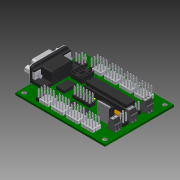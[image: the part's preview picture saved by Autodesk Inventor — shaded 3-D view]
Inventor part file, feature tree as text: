
AUTODESK INVENTOR PART (.ipt)
format: ipt  version: 2015 (Build 190159000, 159)  size: 3,395,584 bytes
history: native  units: in
note: dims shown in document units (in); Inventor stores cm internally (conversion verified against a paired STEP export)
features: imported_body x155, other x125, chamfer x18, extrude x11, sketch x2, fillet x1, revolve x1, mirror x1
ambient origin geometry x8: Origin, YZ Plane, XZ Plane, XY Plane, X Axis, Y Axis, Z Axis, Center Point
bodies: Body1 (feature_tree), Body2 (feature_tree), Body3 (feature_tree), Body4 (feature_tree), Body5 (feature_tree), Body6 (feature_tree), Body7 (feature_tree), Body8 (feature_tree), Body9 (feature_tree), Body10 (feature_tree), Body11 (feature_tree), Body12 (feature_tree), Body13 (feature_tree), Body14 (feature_tree), Body15 (feature_tree), Body16 (feature_tree), Body17 (feature_tree), Body18 (feature_tree), Body19 (feature_tree), Body20 (feature_tree), Body21 (feature_tree), Body22 (feature_tree), Body23 (feature_tree), Body24 (feature_tree), Body25 (feature_tree), Body26 (feature_tree), Body27 (feature_tree), Body28 (feature_tree), Body29 (feature_tree), Body30 (feature_tree), Body31 (feature_tree), Body32 (feature_tree), Body33 (feature_tree), Body34 (feature_tree), Body35 (feature_tree), Body36 (feature_tree), Body37 (feature_tree), Body38 (feature_tree), Body39 (feature_tree), Body40 (feature_tree), Body41 (feature_tree), Body42 (feature_tree), Body43 (feature_tree), Body44 (feature_tree), Body45 (feature_tree), Body46 (feature_tree), Body47 (feature_tree), Body48 (feature_tree), Body49 (feature_tree), Body50 (feature_tree), Body51 (feature_tree), Body52 (feature_tree), Body53 (feature_tree), Body54 (feature_tree), Body55 (feature_tree), Body56 (feature_tree), Body57 (feature_tree), Body58 (feature_tree), Body59 (feature_tree), Body60 (feature_tree), Body61 (feature_tree), Body62 (feature_tree), Body63 (feature_tree), Body64 (feature_tree), Body65 (feature_tree), Body66 (feature_tree), Body67 (feature_tree), Body68 (feature_tree), Body69 (feature_tree), Body70 (feature_tree), Body71 (feature_tree), Body72 (feature_tree), Body73 (feature_tree), Body74 (feature_tree), Body75 (feature_tree), Body76 (feature_tree), Body77 (feature_tree), Body78 (feature_tree), Body79 (feature_tree), Body80 (feature_tree), Body81 (feature_tree), Body82 (feature_tree), Body83 (feature_tree), Body84 (feature_tree), Body85 (feature_tree), Body86 (feature_tree), Body87 (feature_tree), Body88 (feature_tree), Body89 (feature_tree), Body90 (feature_tree), Body91 (feature_tree), Body92 (feature_tree), Body93 (feature_tree), Body94 (feature_tree), Body95 (feature_tree), Body96 (feature_tree), Body97 (feature_tree), Body98 (feature_tree), Body99 (feature_tree), Body100 (feature_tree), Body101 (feature_tree), Body102 (feature_tree), Body103 (feature_tree), Body104 (feature_tree), Body105 (feature_tree), Body106 (feature_tree), Body107 (feature_tree), Body108 (feature_tree), Body109 (feature_tree), Body110 (feature_tree), Body111 (feature_tree), Body112 (feature_tree), Body113 (feature_tree), Body114 (feature_tree), Body115 (feature_tree), Body116 (feature_tree), Body117 (feature_tree), Body118 (feature_tree), Body119 (feature_tree), Body120 (feature_tree), Body121 (feature_tree), Body122 (feature_tree), Body123 (feature_tree), Body124 (feature_tree), Body125 (feature_tree), Body126 (feature_tree), Body127 (feature_tree), Body128 (feature_tree), Body129 (feature_tree), Body130 (feature_tree), Body131 (feature_tree), Body132 (feature_tree), Body133 (feature_tree), Body134 (feature_tree), Body135 (feature_tree), Body136 (feature_tree), Body137 (feature_tree), Body138 (feature_tree), Body139 (feature_tree), Body140 (feature_tree), Body141 (feature_tree), Body142 (feature_tree), Body143 (feature_tree), Body144 (feature_tree), Body145 (feature_tree), Body146 (feature_tree), Body147 (feature_tree), Body148 (feature_tree), Body149 (feature_tree), Body150 (feature_tree), Body151 (feature_tree), Body152 (feature_tree), Body153 (feature_tree), Body154 (feature_tree), Body155 (feature_tree)
feature tree (314):
  chamfer  "Chamfer1"  Distance=1.0039in
  other  "ssc-321"
  sketch  "Sketch1"  dims[d2=0.1378in]
  extrude  "Extrusion1"  Depth=1.0in
  chamfer  "Chamfer2"  Distance=0.1378in
  other  "LPattern2[4]"
  other  "LPattern2[5]"
  other  "LPattern2[6]"
  other  "LPattern2[7]"
  other  "LPattern2[8]"
  other  "LPattern2[9]"
  other  "LPattern2[10]"
  other  "LPattern2[11]"
  other  "LPattern2[12]"
  other  "LPattern2[13]"
  other  "LPattern2[14]"
  other  "LPattern2[15]"
  other  "LPattern2[16]"
  other  "LPattern2[20]"
  other  "LPattern2[21]"
  other  "LPattern2[22]"
  other  "LPattern2[23]"
  other  "LPattern2[24]"
  other  "LPattern2[25]"
  other  "LPattern2[26]"
  other  "LPattern2[27]"
  other  "LPattern2[28]"
  other  "LPattern2[29]"
  other  "LPattern2[30]"
  other  "LPattern2[31]"
  other  "LPattern2[32]"
  other  "LPattern2[36]"
  other  "LPattern2[37]"
  other  "LPattern2[38]"
  other  "LPattern2[39]"
  other  "LPattern2[40]"
  other  "LPattern2[41]"
  other  "LPattern2[42]"
  other  "LPattern2[43]"
  other  "LPattern2[44]"
  other  "LPattern2[45]"
  other  "LPattern2[46]"
  other  "LPattern2[47]"
  chamfer  "Chamfer5"  Distance=1.0039in
  chamfer  "Chamfer6"  Distance=1.0039in
  chamfer  "Chamfer9"  Distance=1.348in
  chamfer  "Chamfer10"  Distance=1.348in
  other  "LPattern3"
  other  "LPattern4[1]"
  other  "LPattern4[2]"
  other  "LPattern4[3]"
  other  "LPattern4[4]"
  other  "LPattern4[5]"
  other  "LPattern4[6]"
  other  "LPattern4[7]"
  other  "LPattern4[8]"
  other  "LPattern4[9]"
  other  "LPattern4[10]"
  other  "LPattern4[11]"
  other  "LPattern4[12]"
  other  "LPattern4[13]"
  other  "LPattern4[14]"
  other  "LPattern4[15]"
  other  "LPattern4[16]"
  other  "LPattern4[17]"
  other  "LPattern4[18]"
  other  "LPattern4[19]"
  other  "LPattern4[20]"
  other  "LPattern4[21]"
  other  "LPattern4[22]"
  other  "LPattern4[23]"
  other  "LPattern4[24]"
  other  "LPattern4[25]"
  other  "LPattern4[26]"
  other  "LPattern4[27]"
  other  "LPattern4[28]"
  other  "LPattern4[29]"
  other  "LPattern4[30]"
  other  "LPattern4[31]"
  other  "LPattern4[32]"
  other  "LPattern4[33]"
  other  "LPattern4[34]"
  other  "LPattern4[35]"
  other  "LPattern4[36]"
  other  "LPattern4[37]"
  other  "LPattern4[38]"
  other  "LPattern4[39]"
  other  "LPattern4[40]"
  other  "LPattern4[41]"
  other  "LPattern4[42]"
  other  "LPattern4[43]"
  other  "LPattern4[44]"
  other  "LPattern4[45]"
  other  "LPattern4[46]"
  other  "LPattern4[47]"
  extrude  "Extrude4[1]"  Depth=1.348in
  extrude  "Extrude4[2]"  Depth=1.348in
  extrude  "Extrude4[4]"  Depth=1.0in TaperAngle=0.0deg
  extrude  "Extrude4[3]"  [1 undecoded]
  other  "#4-40 Tapped Hole1[1]"
  other  "#4-40 Tapped Hole1[2]"
  other  "#4-40 Tapped Hole1[3]"
  other  "#4-40 Tapped Hole1[4]"
  chamfer  "Chamfer7"  [1 undecoded]
  chamfer  "Chamfer8"  [1 undecoded]
  chamfer  "Chamfer11"  [1 undecoded]
  chamfer  "Chamfer12"  [1 undecoded]
  other  "LPattern5[1]"
  other  "LPattern5[2]"
  other  "LPattern5[3]"
  other  "LPattern5[4]"
  other  "LPattern5[5]"
  other  "LPattern5[6]"
  other  "LPattern5[7]"
  other  "LPattern5[8]"
  chamfer  "Chamfer13"  [1 undecoded]
  chamfer  "Chamfer14"  [1 undecoded]
  chamfer  "Chamfer15"  [1 undecoded]
  other  "LPattern6[1]"
  other  "LPattern6[2]"
  other  "LPattern6[3]"
  other  "LPattern6[4]"
  other  "LPattern6[5]"
  other  "LPattern6[6]"
  other  "LPattern6[7]"
  other  "LPattern6[8]"
  other  "LPattern6[9]"
  other  "LPattern6[10]"
  other  "LPattern6[11]"
  other  "LPattern6[12]"
  other  "LPattern6[13]"
  other  "LPattern6[14]"
  other  "LPattern6[15]"
  extrude  "Extrude16"  [1 undecoded]
  other  "Cut-Extrude2"
  other  "LPattern9"
  fillet  "Fillet6"  [1 undecoded]
  extrude  "Extrude21"  [1 undecoded]
  extrude  "Extrude22"  [1 undecoded]
  other  "Cut-Extrude7"
  other  "LPattern10[1]"
  other  "LPattern10[2]"
  other  "LPattern10[3]"
  extrude  "Extrude24"  [1 undecoded]
  chamfer  "Chamfer16"  [1 undecoded]
  chamfer  "Chamfer17"  [1 undecoded]
  chamfer  "Chamfer18"  [1 undecoded]
  other  "LPattern11[1]"
  other  "LPattern11[2]"
  other  "LPattern11[3]"
  chamfer  "Chamfer19"  [1 undecoded]
  chamfer  "Chamfer20"  [1 undecoded]
  other  "LPattern12[1]"
  other  "LPattern12[2]"
  revolve  "Revolve1"  [1 undecoded]
  mirror  "Mirror1"
  extrude  "Extrude29[1]"  [1 undecoded]
  extrude  "Extrude29[2]"  [1 undecoded]
  imported_body  "Base1"
  imported_body  "Base2"
  imported_body  "Base3"
  imported_body  "Base4"
  imported_body  "Base5"
  imported_body  "Base6"
  imported_body  "Base7"
  imported_body  "Base8"
  imported_body  "Base9"
  imported_body  "Base10"
  imported_body  "Base11"
  imported_body  "Base12"
  imported_body  "Base13"
  imported_body  "Base14"
  imported_body  "Base15"
  imported_body  "Base16"
  imported_body  "Base17"
  imported_body  "Base18"
  imported_body  "Base19"
  imported_body  "Base20"
  imported_body  "Base21"
  imported_body  "Base22"
  imported_body  "Base23"
  imported_body  "Base24"
  imported_body  "Base25"
  imported_body  "Base26"
  imported_body  "Base27"
  imported_body  "Base28"
  imported_body  "Base29"
  imported_body  "Base30"
  imported_body  "Base31"
  imported_body  "Base32"
  imported_body  "Base33"
  imported_body  "Base34"
  imported_body  "Base35"
  imported_body  "Base36"
  imported_body  "Base37"
  imported_body  "Base38"
  imported_body  "Base39"
  imported_body  "Base40"
  imported_body  "Base41"
  imported_body  "Base42"
  imported_body  "Base43"
  imported_body  "Base44"
  imported_body  "Base45"
  imported_body  "Base46"
  imported_body  "Base47"
  imported_body  "Base48"
  imported_body  "Base49"
  imported_body  "Base50"
  imported_body  "Base51"
  imported_body  "Base52"
  imported_body  "Base53"
  imported_body  "Base54"
  imported_body  "Base55"
  imported_body  "Base56"
  imported_body  "Base57"
  imported_body  "Base58"
  imported_body  "Base59"
  imported_body  "Base60"
  imported_body  "Base61"
  imported_body  "Base62"
  imported_body  "Base63"
  imported_body  "Base64"
  imported_body  "Base65"
  imported_body  "Base66"
  imported_body  "Base67"
  imported_body  "Base68"
  imported_body  "Base69"
  imported_body  "Base70"
  imported_body  "Base71"
  imported_body  "Base72"
  imported_body  "Base73"
  imported_body  "Base74"
  imported_body  "Base75"
  imported_body  "Base76"
  imported_body  "Base77"
  imported_body  "Base78"
  imported_body  "Base79"
  imported_body  "Base80"
  imported_body  "Base81"
  imported_body  "Base82"
  imported_body  "Base83"
  imported_body  "Base84"
  imported_body  "Base85"
  imported_body  "Base86"
  imported_body  "Base87"
  imported_body  "Base88"
  imported_body  "Base89"
  imported_body  "Base90"
  imported_body  "Base91"
  imported_body  "Base92"
  imported_body  "Base93"
  imported_body  "Base94"
  imported_body  "Base95"
  imported_body  "Base96"
  imported_body  "Base97"
  imported_body  "Base98"
  imported_body  "Base99"
  imported_body  "Base100"
  imported_body  "Base101"
  imported_body  "Base102"
  imported_body  "Base103"
  imported_body  "Base104"
  imported_body  "Base105"
  imported_body  "Base106"
  imported_body  "Base107"
  imported_body  "Base108"
  imported_body  "Base109"
  imported_body  "Base110"
  imported_body  "Base111"
  imported_body  "Base112"
  imported_body  "Base113"
  imported_body  "Base114"
  imported_body  "Base115"
  imported_body  "Base116"
  imported_body  "Base117"
  imported_body  "Base118"
  imported_body  "Base119"
  imported_body  "Base120"
  imported_body  "Base121"
  imported_body  "Base122"
  imported_body  "Base123"
  imported_body  "Base124"
  imported_body  "Base125"
  imported_body  "Base126"
  imported_body  "Base127"
  imported_body  "Base128"
  imported_body  "Base129"
  imported_body  "Base130"
  imported_body  "Base131"
  imported_body  "Base132"
  imported_body  "Base133"
  imported_body  "Base134"
  imported_body  "Base135"
  imported_body  "Base136"
  imported_body  "Base137"
  imported_body  "Base138"
  imported_body  "Base139"
  imported_body  "Base140"
  imported_body  "Base141"
  imported_body  "Base142"
  imported_body  "Base143"
  imported_body  "Base144"
  imported_body  "Base145"
  imported_body  "Base146"
  imported_body  "Base147"
  imported_body  "Base148"
  imported_body  "Base149"
  imported_body  "Base150"
  imported_body  "Base151"
  imported_body  "Base152"
  imported_body  "Base153"
  imported_body  "Base154"
  imported_body  "Base155"
  sketch  "Sketch2"  dims[d3=0.1378in d4=1.0039in d5=1.0039in d6=0.1378in d8=1.0039in d9=1.0039in d12=1.348in d13=1.348in d14=1.348in d15=1.348in d16=1.0in d17=0.0in]
note: 21 required parameter values undecoded (feature->parameter linkage not recoverable at this tier; creation-order binding heuristic only, values carry confidence <= 0.55)
